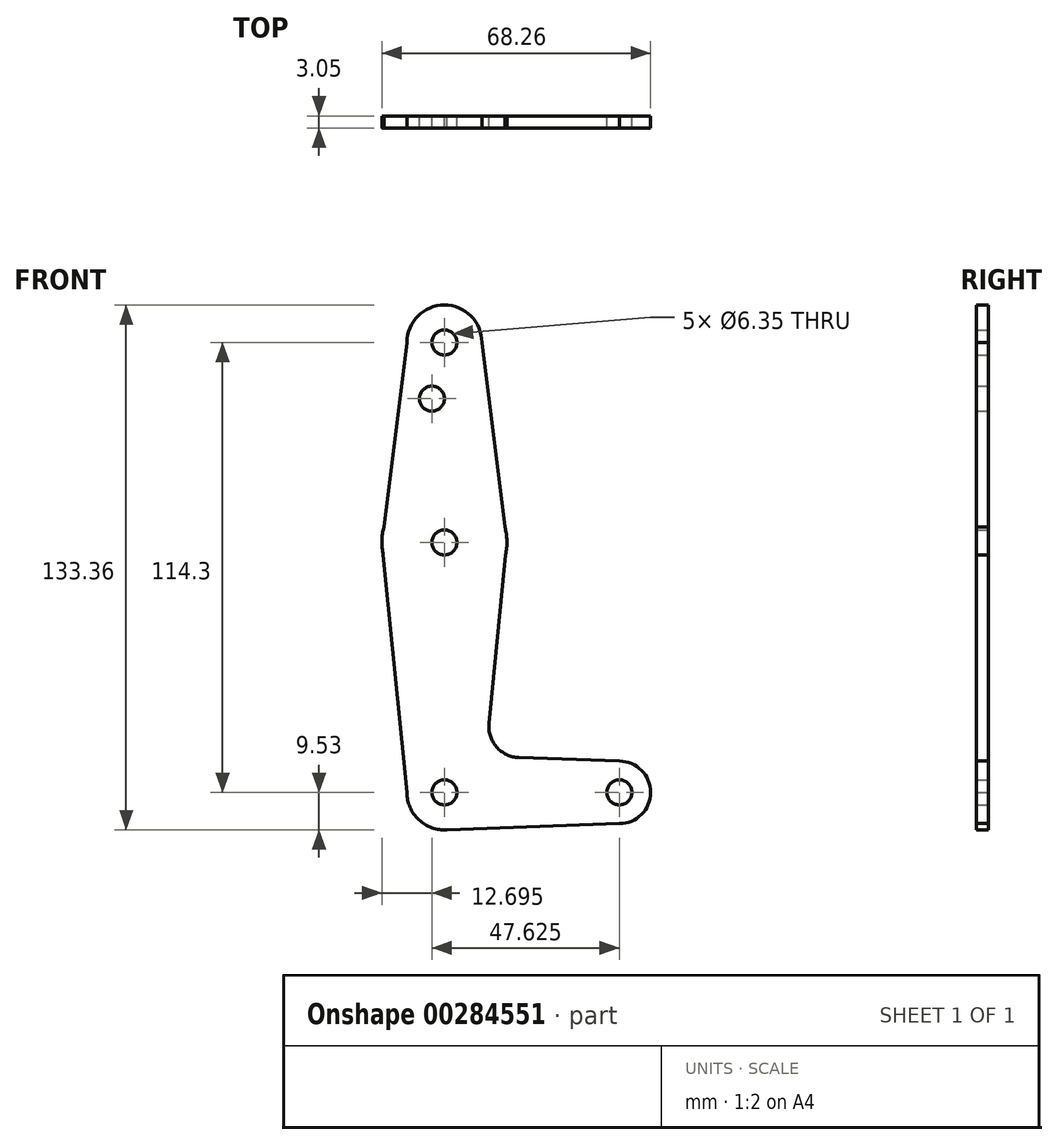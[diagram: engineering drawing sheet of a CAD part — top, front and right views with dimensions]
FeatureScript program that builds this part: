
annotation { "Feature Type Name" : "Feature", "Feature Type Description" : "" }
export const myFeature = defineFeature(function(context is Context, id is Id, definition is map)
    precondition{}
    {
        {
            var Q0;
            Q0=qCreatedBy(makeId("Front.planeOp"),FACE);
            var sketch = newSketch(context, id + "F0", { "sketchPlane" : qUnion([Q0])});
            skLineSegment(sketch, "E0", {"start": v(44.45, 0) * mm, "end": v(0, 0) * mm, "construction": true});
            skLineSegment(sketch, "E1", {"start": v(0, 0) * mm, "end": v(0, 63.5) * mm, "construction": true});
            skLineSegment(sketch, "E2", {"start": v(0, 63.5) * mm, "end": v(0, 114.3) * mm, "construction": true});
            skCircle(sketch, "E3", {"center": v(0, 114.3) * mm, "radius": 9.53 * mm});
            skCircle(sketch, "E4", {"center": v(0, 63.5) * mm, "radius": 15.88 * mm});
            skCircle(sketch, "E5", {"center": v(0, 0) * mm, "radius": 9.53 * mm});
            skCircle(sketch, "E6", {"center": v(44.45, 0) * mm, "radius": 7.94 * mm});
            skLineSegment(sketch, "E7", {"start": v(-9.52, 114.3) * mm, "end": v(-15.88, 63.5) * mm});
            skLineSegment(sketch, "E8", {"start": v(9.52, 114.3) * mm, "end": v(15.88, 63.5) * mm});
            skLineSegment(sketch, "E9", {"start": v(18.94, 8.85) * mm, "end": v(44.45, 7.94) * mm});
            skLineSegment(sketch, "E10", {"start": v(0, -9.53) * mm, "end": v(44.45, -7.94) * mm});
            skLineSegment(sketch, "E11", {"start": v(-15.88, 63.5) * mm, "end": v(-9.52, 0) * mm});
            skCircle(sketch, "E12", {"center": v(0, 114.3) * mm, "radius": 3.18 * mm});
            skCircle(sketch, "E13", {"center": v(0, 63.5) * mm, "radius": 3.18 * mm});
            skCircle(sketch, "E14", {"center": v(0, 0) * mm, "radius": 3.18 * mm});
            skCircle(sketch, "E15", {"center": v(44.45, 0) * mm, "radius": 3.18 * mm});
            skCircle(sketch, "E16", {"center": v(-3.18, 100.03) * mm, "radius": 3.18 * mm});
            skLineSegment(sketch, "E17", {"start": v(15.88, 63.5) * mm, "end": v(11.32, 17.58) * mm});
            skPoint(sketch, "E18.newPointA", {"position": v(9.57, 0) * mm});
            skArc(sketch, "E18.filletArc", {"start": v(11.32, 17.58) * mm, "mid": v(13.24, 11.56) * mm, "end": v(18.94, 8.85) * mm});
            skSolve(sketch);
        }
        {
            var Q0;
            Q0 = qSketchRegion(id + "F0", true);
            extrude(context, id + "F1", {"entities" : qUnion([Q0]), "depth" : 3.05 * mm});
        }
    });
